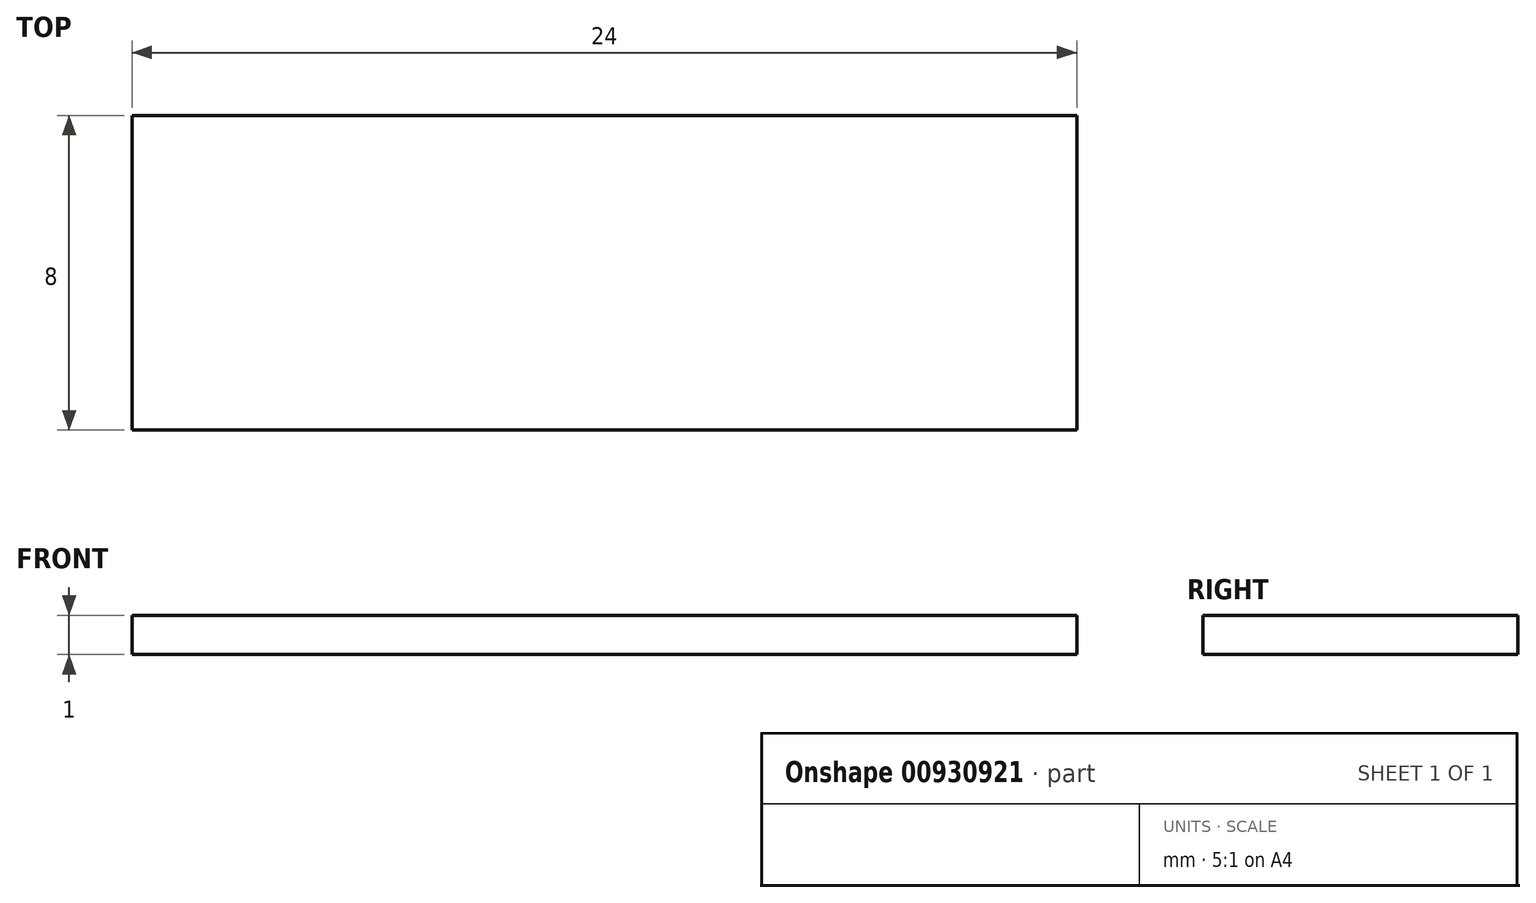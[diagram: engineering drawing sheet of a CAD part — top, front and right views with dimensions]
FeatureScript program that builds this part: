
annotation { "Feature Type Name" : "Feature", "Feature Type Description" : "" }
export const myFeature = defineFeature(function(context is Context, id is Id, definition is map)
    precondition{}
    {
        {
            var Q0;
            Q0=qCreatedBy(makeId("Top.planeOp"),FACE);
            var sketch = newSketch(context, id + "F0", { "sketchPlane" : qUnion([Q0])});
            skLineSegment(sketch, "E0.bottom", {"start": v(12, 4) * mm, "end": v(-12, 4) * mm});
            skLineSegment(sketch, "E0.top", {"start": v(12, -4) * mm, "end": v(-12, -4) * mm});
            skLineSegment(sketch, "E0.left", {"start": v(12, 4) * mm, "end": v(12, -4) * mm});
            skLineSegment(sketch, "E0.right", {"start": v(-12, 4) * mm, "end": v(-12, -4) * mm});
            skPoint(sketch, "E0.middle", {"position": v(0, 0) * mm});
            skSolve(sketch);
        }
        {
            var Q0;
            Q0=makeQuery(id+"F0.imprint","IMPRINT",FACE,{"disambiguationData":[TD([[makeQuery(id+"F0.imprint","IMPRINT",EDGE,{"derivedFrom":sQuery(id+"F0.wireOp",EDGE,"E0.bottom")}),1.0]])]});
            extrude(context, id + "F1", {"entities" : qUnion([Q0]), "depth" : 1 * mm, "offsetDistance" : 25 * mm});
        }
    });
